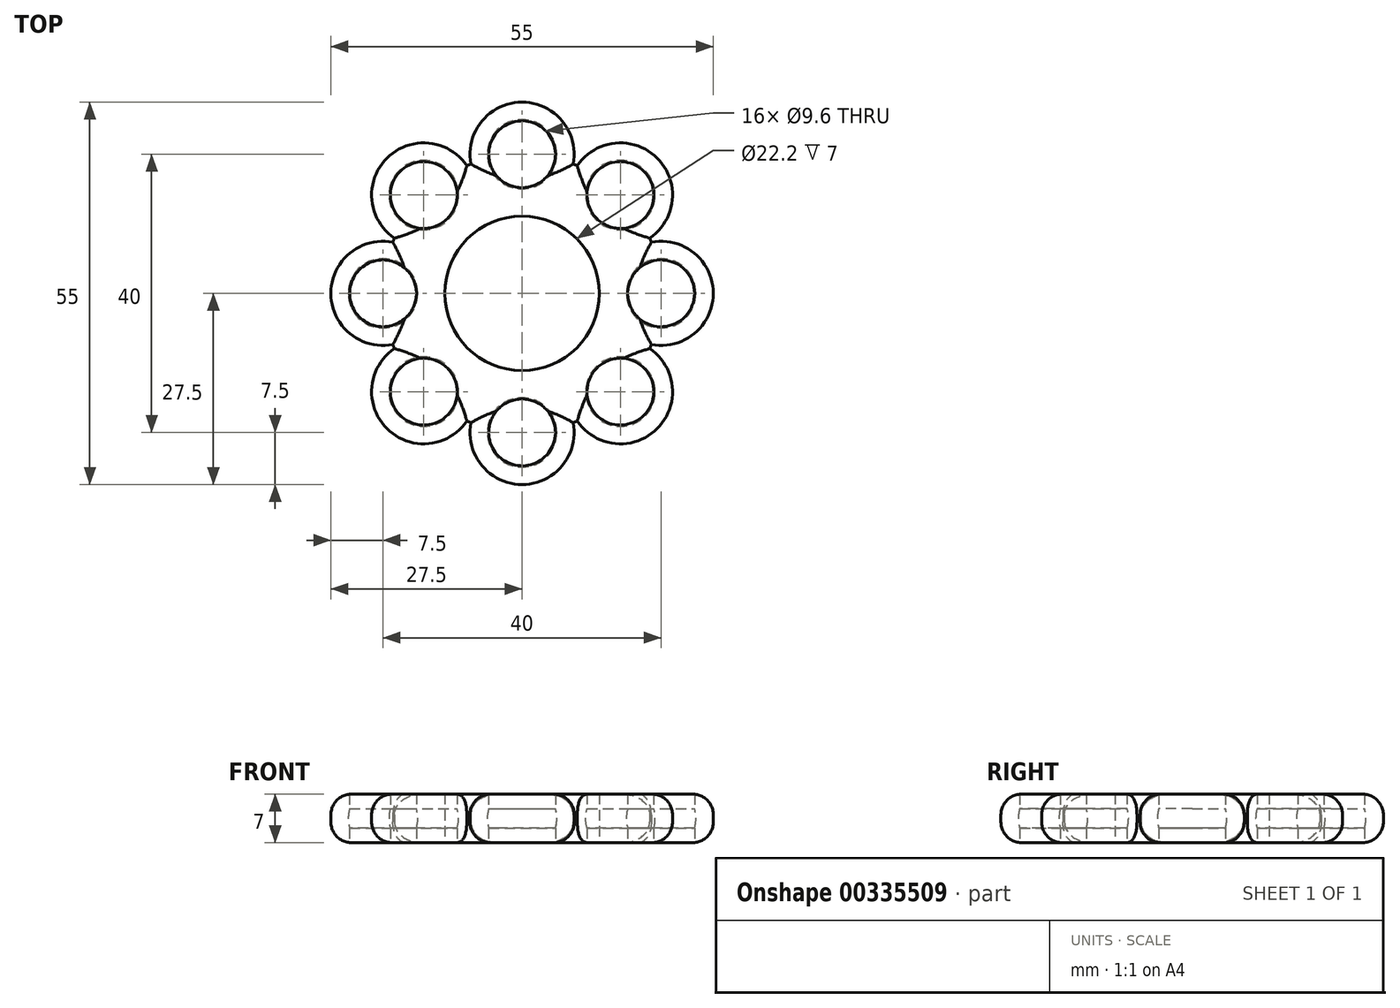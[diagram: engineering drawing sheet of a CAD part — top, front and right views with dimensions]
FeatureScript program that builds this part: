
annotation { "Feature Type Name" : "Feature", "Feature Type Description" : "" }
export const myFeature = defineFeature(function(context is Context, id is Id, definition is map)
    precondition{}
    {
        {
            var Q0;
            Q0=qCreatedBy(makeId("Top.planeOp"),FACE);
            var sketch = newSketch(context, id + "F0", { "sketchPlane" : qUnion([Q0])});
            skCircle(sketch, "E0", {"center": v(0, 0) * mm, "radius": 11.1 * mm});
            skCircle(sketch, "E1", {"center": v(0, 20) * mm, "radius": 4.8 * mm});
            skCircle(sketch, "E2.1.0", {"center": v(-14.14, 14.14) * mm, "radius": 4.8 * mm});
            skCircle(sketch, "E2.2.0", {"center": v(-20, 0) * mm, "radius": 4.8 * mm});
            skCircle(sketch, "E2.3.0", {"center": v(-14.14, -14.14) * mm, "radius": 4.8 * mm});
            skCircle(sketch, "E2.4.0", {"center": v(0, -20) * mm, "radius": 4.8 * mm});
            skCircle(sketch, "E2.5.0", {"center": v(14.14, -14.14) * mm, "radius": 4.8 * mm});
            skCircle(sketch, "E2.6.0", {"center": v(20, 0) * mm, "radius": 4.8 * mm});
            skCircle(sketch, "E2.7.0", {"center": v(14.14, 14.14) * mm, "radius": 4.8 * mm});
            skCircle(sketch, "E3", {"center": v(0, 20) * mm, "radius": 7.5 * mm});
            skCircle(sketch, "E4.1.0", {"center": v(-14.14, 14.14) * mm, "radius": 7.5 * mm});
            skCircle(sketch, "E4.2.0", {"center": v(-20, 0) * mm, "radius": 7.5 * mm});
            skCircle(sketch, "E4.3.0", {"center": v(-14.14, -14.14) * mm, "radius": 7.5 * mm});
            skCircle(sketch, "E4.4.0", {"center": v(0, -20) * mm, "radius": 7.5 * mm});
            skCircle(sketch, "E4.5.0", {"center": v(14.14, -14.14) * mm, "radius": 7.5 * mm});
            skCircle(sketch, "E4.6.0", {"center": v(20, 0) * mm, "radius": 7.5 * mm});
            skCircle(sketch, "E4.7.0", {"center": v(14.14, 14.14) * mm, "radius": 7.5 * mm});
            skCircle(sketch, "E5", {"center": v(0, 0) * mm, "radius": 20 * mm});
            skSolve(sketch);
        }
        {
            var Q0;
            Q0=makeQuery(id+"F0.imprint","IMPRINT",FACE,{"disambiguationData":[TD([[makeQuery(id+"F0.imprint","IMPRINT",EDGE,{"derivedFrom":sQuery(id+"F0.wireOp",EDGE,"E0")}),-1.0]])]});
            var Q1;
            {var subQ0=sQuery(id+"F0.wireOp",EDGE,"E5");var subQ1=sQuery(id+"F0.wireOp",EDGE,"E2.3.0");var subQ2=makeQuery(id+"F0.imprint","INTERSECT",VERTEX,{"disambiguationData":[OD(0.0)],"derivedFrom":[subQ1,subQ0]});Q1=makeQuery(id+"F0.imprint","IMPRINT",FACE,{"disambiguationData":[TD([[makeQuery(id+"F0.imprint","IMPRINT",EDGE,{"disambiguationData":[TD([[subQ2,-1.0]])],"derivedFrom":subQ1}),-1.0]])]});}
            var Q2;
            {var subQ0=sQuery(id+"F0.wireOp",EDGE,"E5");var subQ1=sQuery(id+"F0.wireOp",EDGE,"E2.3.0");var subQ2=makeQuery(id+"F0.imprint","INTERSECT",VERTEX,{"disambiguationData":[OD(0.0)],"derivedFrom":[subQ1,subQ0]});Q2=makeQuery(id+"F0.imprint","IMPRINT",FACE,{"disambiguationData":[TD([[makeQuery(id+"F0.imprint","IMPRINT",EDGE,{"disambiguationData":[TD([[subQ2,1.0]])],"derivedFrom":subQ1}),-1.0]])]});}
            var Q3;
            {var subQ0=sQuery(id+"F0.wireOp",EDGE,"E5");var subQ1=sQuery(id+"F0.wireOp",EDGE,"E2.2.0");var subQ2=makeQuery(id+"F0.imprint","INTERSECT",VERTEX,{"disambiguationData":[OD(0.0)],"derivedFrom":[subQ1,subQ0]});Q3=makeQuery(id+"F0.imprint","IMPRINT",FACE,{"disambiguationData":[TD([[makeQuery(id+"F0.imprint","IMPRINT",EDGE,{"disambiguationData":[TD([[subQ2,1.0]])],"derivedFrom":subQ1}),-1.0]])]});}
            var Q4;
            {var subQ0=sQuery(id+"F0.wireOp",EDGE,"E5");var subQ1=sQuery(id+"F0.wireOp",EDGE,"E2.2.0");var subQ2=makeQuery(id+"F0.imprint","INTERSECT",VERTEX,{"disambiguationData":[OD(0.0)],"derivedFrom":[subQ1,subQ0]});Q4=makeQuery(id+"F0.imprint","IMPRINT",FACE,{"disambiguationData":[TD([[makeQuery(id+"F0.imprint","IMPRINT",EDGE,{"disambiguationData":[TD([[subQ2,-1.0]])],"derivedFrom":subQ1}),-1.0]])]});}
            var Q5;
            {var subQ0=sQuery(id+"F0.wireOp",EDGE,"E5");var subQ1=sQuery(id+"F0.wireOp",EDGE,"E2.1.0");var subQ2=makeQuery(id+"F0.imprint","INTERSECT",VERTEX,{"disambiguationData":[OD(0.0)],"derivedFrom":[subQ1,subQ0]});Q5=makeQuery(id+"F0.imprint","IMPRINT",FACE,{"disambiguationData":[TD([[makeQuery(id+"F0.imprint","IMPRINT",EDGE,{"disambiguationData":[TD([[subQ2,-1.0]])],"derivedFrom":subQ1}),-1.0]])]});}
            var Q6;
            {var subQ0=sQuery(id+"F0.wireOp",EDGE,"E5");var subQ1=sQuery(id+"F0.wireOp",EDGE,"E2.1.0");var subQ2=makeQuery(id+"F0.imprint","INTERSECT",VERTEX,{"disambiguationData":[OD(0.0)],"derivedFrom":[subQ1,subQ0]});Q6=makeQuery(id+"F0.imprint","IMPRINT",FACE,{"disambiguationData":[TD([[makeQuery(id+"F0.imprint","IMPRINT",EDGE,{"disambiguationData":[TD([[subQ2,1.0]])],"derivedFrom":subQ1}),-1.0]])]});}
            var Q7;
            {var subQ0=sQuery(id+"F0.wireOp",EDGE,"E5");var subQ1=sQuery(id+"F0.wireOp",EDGE,"E1");var subQ2=makeQuery(id+"F0.imprint","INTERSECT",VERTEX,{"disambiguationData":[OD(0.0)],"derivedFrom":[subQ1,subQ0]});Q7=makeQuery(id+"F0.imprint","IMPRINT",FACE,{"disambiguationData":[TD([[makeQuery(id+"F0.imprint","IMPRINT",EDGE,{"disambiguationData":[TD([[subQ2,1.0]])],"derivedFrom":subQ1}),-1.0]])]});}
            var Q8;
            {var subQ0=sQuery(id+"F0.wireOp",EDGE,"E5");var subQ1=sQuery(id+"F0.wireOp",EDGE,"E1");var subQ2=makeQuery(id+"F0.imprint","INTERSECT",VERTEX,{"disambiguationData":[OD(0.0)],"derivedFrom":[subQ1,subQ0]});Q8=makeQuery(id+"F0.imprint","IMPRINT",FACE,{"disambiguationData":[TD([[makeQuery(id+"F0.imprint","IMPRINT",EDGE,{"disambiguationData":[TD([[subQ2,-1.0]])],"derivedFrom":subQ1}),-1.0]])]});}
            var Q9;
            {var subQ0=sQuery(id+"F0.wireOp",EDGE,"E5");var subQ1=sQuery(id+"F0.wireOp",EDGE,"E2.7.0");var subQ2=makeQuery(id+"F0.imprint","INTERSECT",VERTEX,{"disambiguationData":[OD(0.0)],"derivedFrom":[subQ1,subQ0]});Q9=makeQuery(id+"F0.imprint","IMPRINT",FACE,{"disambiguationData":[TD([[makeQuery(id+"F0.imprint","IMPRINT",EDGE,{"disambiguationData":[TD([[subQ2,1.0]])],"derivedFrom":subQ1}),-1.0]])]});}
            var Q10;
            {var subQ0=sQuery(id+"F0.wireOp",EDGE,"E5");var subQ1=sQuery(id+"F0.wireOp",EDGE,"E2.7.0");var subQ2=makeQuery(id+"F0.imprint","INTERSECT",VERTEX,{"disambiguationData":[OD(0.0)],"derivedFrom":[subQ1,subQ0]});Q10=makeQuery(id+"F0.imprint","IMPRINT",FACE,{"disambiguationData":[TD([[makeQuery(id+"F0.imprint","IMPRINT",EDGE,{"disambiguationData":[TD([[subQ2,-1.0]])],"derivedFrom":subQ1}),-1.0]])]});}
            var Q11;
            {var subQ0=sQuery(id+"F0.wireOp",EDGE,"E5");var subQ1=sQuery(id+"F0.wireOp",EDGE,"E2.6.0");var subQ2=makeQuery(id+"F0.imprint","INTERSECT",VERTEX,{"disambiguationData":[OD(0.0)],"derivedFrom":[subQ1,subQ0]});Q11=makeQuery(id+"F0.imprint","IMPRINT",FACE,{"disambiguationData":[TD([[makeQuery(id+"F0.imprint","IMPRINT",EDGE,{"disambiguationData":[TD([[subQ2,-1.0]])],"derivedFrom":subQ1}),-1.0]])]});}
            var Q12;
            {var subQ0=sQuery(id+"F0.wireOp",EDGE,"E5");var subQ1=sQuery(id+"F0.wireOp",EDGE,"E2.6.0");var subQ2=makeQuery(id+"F0.imprint","INTERSECT",VERTEX,{"disambiguationData":[OD(0.0)],"derivedFrom":[subQ1,subQ0]});Q12=makeQuery(id+"F0.imprint","IMPRINT",FACE,{"disambiguationData":[TD([[makeQuery(id+"F0.imprint","IMPRINT",EDGE,{"disambiguationData":[TD([[subQ2,1.0]])],"derivedFrom":subQ1}),-1.0]])]});}
            var Q13;
            {var subQ0=sQuery(id+"F0.wireOp",EDGE,"E5");var subQ1=sQuery(id+"F0.wireOp",EDGE,"E2.5.0");var subQ2=makeQuery(id+"F0.imprint","INTERSECT",VERTEX,{"disambiguationData":[OD(0.0)],"derivedFrom":[subQ1,subQ0]});Q13=makeQuery(id+"F0.imprint","IMPRINT",FACE,{"disambiguationData":[TD([[makeQuery(id+"F0.imprint","IMPRINT",EDGE,{"disambiguationData":[TD([[subQ2,1.0]])],"derivedFrom":subQ1}),-1.0]])]});}
            var Q14;
            {var subQ0=sQuery(id+"F0.wireOp",EDGE,"E5");var subQ1=sQuery(id+"F0.wireOp",EDGE,"E2.5.0");var subQ2=makeQuery(id+"F0.imprint","INTERSECT",VERTEX,{"disambiguationData":[OD(0.0)],"derivedFrom":[subQ1,subQ0]});Q14=makeQuery(id+"F0.imprint","IMPRINT",FACE,{"disambiguationData":[TD([[makeQuery(id+"F0.imprint","IMPRINT",EDGE,{"disambiguationData":[TD([[subQ2,-1.0]])],"derivedFrom":subQ1}),-1.0]])]});}
            var Q15;
            {var subQ0=sQuery(id+"F0.wireOp",EDGE,"E5");var subQ1=sQuery(id+"F0.wireOp",EDGE,"E2.4.0");var subQ2=makeQuery(id+"F0.imprint","INTERSECT",VERTEX,{"disambiguationData":[OD(0.0)],"derivedFrom":[subQ1,subQ0]});Q15=makeQuery(id+"F0.imprint","IMPRINT",FACE,{"disambiguationData":[TD([[makeQuery(id+"F0.imprint","IMPRINT",EDGE,{"disambiguationData":[TD([[subQ2,1.0]])],"derivedFrom":subQ1}),-1.0]])]});}
            var Q16;
            {var subQ0=sQuery(id+"F0.wireOp",EDGE,"E5");var subQ1=sQuery(id+"F0.wireOp",EDGE,"E2.4.0");var subQ2=makeQuery(id+"F0.imprint","INTERSECT",VERTEX,{"disambiguationData":[OD(0.0)],"derivedFrom":[subQ1,subQ0]});Q16=makeQuery(id+"F0.imprint","IMPRINT",FACE,{"disambiguationData":[TD([[makeQuery(id+"F0.imprint","IMPRINT",EDGE,{"disambiguationData":[TD([[subQ2,-1.0]])],"derivedFrom":subQ1}),-1.0]])]});}
            extrude(context, id + "F1", {"entities" : qUnion([Q0, Q1, Q2, Q3, Q4, Q5, Q6, Q7, Q8, Q9, Q10, Q11, Q12, Q13, Q14, Q15, Q16]), "depth" : 3.5 * mm, "hasSecondDirection" : true, "secondDirectionOppositeDirection" : true, "secondDirectionDepth" : 3.5 * mm});
        }
        {
            var Q0;
            Q0=makeQuery(id+"F1.opExtrude","CAP_EDGE",EDGE,{"disambiguationData":[OSD([sQuery(id+"F0.wireOp",EDGE,"E4.7.0")])],"isStart":false});
            var Q1;
            Q1=makeQuery(id+"F1.opExtrude","CAP_EDGE",EDGE,{"disambiguationData":[OSD([sQuery(id+"F0.wireOp",EDGE,"E4.7.0")])],"isStart":true});
            var Q2;
            Q2=makeQuery(id+"F1.opExtrude","CAP_EDGE",EDGE,{"disambiguationData":[OSD([sQuery(id+"F0.wireOp",EDGE,"E3")])],"isStart":false});
            var Q3;
            {var subQ0=sQuery(id+"F0.wireOp",EDGE,"E5");Q3=makeQuery(id+"F1.opExtrude","CAP_EDGE",EDGE,{"disambiguationData":[OSD([subQ0]),TDD([makeQuery(id+"F0.imprint","IMPRINT",EDGE,{"disambiguationData":[TD([[makeQuery(id+"F0.imprint","INTERSECT",VERTEX,{"disambiguationData":[OD(0.0)],"derivedFrom":[sQuery(id+"F0.wireOp",EDGE,"E3"),subQ0]}),1.0]])],"derivedFrom":subQ0})])],"isStart":false});}
            var Q4;
            Q4=makeQuery(id+"F1.opExtrude","CAP_EDGE",EDGE,{"disambiguationData":[OSD([sQuery(id+"F0.wireOp",EDGE,"E4.6.0")])],"isStart":false});
            var Q5;
            {var subQ0=sQuery(id+"F0.wireOp",EDGE,"E5");Q5=makeQuery(id+"F1.opExtrude","CAP_EDGE",EDGE,{"disambiguationData":[OSD([subQ0]),TDD([makeQuery(id+"F0.imprint","IMPRINT",EDGE,{"disambiguationData":[TD([[makeQuery(id+"F0.imprint","INTERSECT",VERTEX,{"disambiguationData":[OD(0.0)],"derivedFrom":[sQuery(id+"F0.wireOp",EDGE,"E4.6.0"),subQ0]}),-1.0]])],"derivedFrom":subQ0})])],"isStart":false});}
            var Q6;
            Q6=makeQuery(id+"F1.opExtrude","CAP_EDGE",EDGE,{"disambiguationData":[OSD([sQuery(id+"F0.wireOp",EDGE,"E4.1.0")])],"isStart":false});
            var Q7;
            {var subQ0=sQuery(id+"F0.wireOp",EDGE,"E5");Q7=makeQuery(id+"F1.opExtrude","CAP_EDGE",EDGE,{"disambiguationData":[OSD([subQ0]),TDD([makeQuery(id+"F0.imprint","IMPRINT",EDGE,{"disambiguationData":[TD([[makeQuery(id+"F0.imprint","INTERSECT",VERTEX,{"disambiguationData":[OD(1.0)],"derivedFrom":[sQuery(id+"F0.wireOp",EDGE,"E3"),subQ0]}),-1.0]])],"derivedFrom":subQ0})])],"isStart":false});}
            var Q8;
            Q8=makeQuery(id+"F1.opExtrude","CAP_EDGE",EDGE,{"disambiguationData":[OSD([sQuery(id+"F0.wireOp",EDGE,"E4.2.0")])],"isStart":false});
            var Q9;
            Q9=makeQuery(id+"F1.opExtrude","CAP_EDGE",EDGE,{"disambiguationData":[OSD([sQuery(id+"F0.wireOp",EDGE,"E4.3.0")])],"isStart":false});
            var Q10;
            Q10=makeQuery(id+"F1.opExtrude","CAP_EDGE",EDGE,{"disambiguationData":[OSD([sQuery(id+"F0.wireOp",EDGE,"E4.4.0")])],"isStart":false});
            var Q11;
            Q11=makeQuery(id+"F1.opExtrude","CAP_EDGE",EDGE,{"disambiguationData":[OSD([sQuery(id+"F0.wireOp",EDGE,"E4.5.0")])],"isStart":false});
            var Q12;
            {var subQ0=sQuery(id+"F0.wireOp",EDGE,"E5");Q12=makeQuery(id+"F1.opExtrude","CAP_EDGE",EDGE,{"disambiguationData":[OSD([subQ0]),TDD([makeQuery(id+"F0.imprint","IMPRINT",EDGE,{"disambiguationData":[TD([[makeQuery(id+"F0.imprint","INTERSECT",VERTEX,{"disambiguationData":[OD(1.0)],"derivedFrom":[sQuery(id+"F0.wireOp",EDGE,"E4.5.0"),subQ0]}),-1.0]])],"derivedFrom":subQ0})])],"isStart":false});}
            var Q13;
            {var subQ0=sQuery(id+"F0.wireOp",EDGE,"E5");Q13=makeQuery(id+"F1.opExtrude","CAP_EDGE",EDGE,{"disambiguationData":[OSD([subQ0]),TDD([makeQuery(id+"F0.imprint","IMPRINT",EDGE,{"disambiguationData":[TD([[makeQuery(id+"F0.imprint","INTERSECT",VERTEX,{"disambiguationData":[OD(1.0)],"derivedFrom":[sQuery(id+"F0.wireOp",EDGE,"E4.4.0"),subQ0]}),-1.0]])],"derivedFrom":subQ0})])],"isStart":false});}
            var Q14;
            {var subQ0=sQuery(id+"F0.wireOp",EDGE,"E5");Q14=makeQuery(id+"F1.opExtrude","CAP_EDGE",EDGE,{"disambiguationData":[OSD([subQ0]),TDD([makeQuery(id+"F0.imprint","IMPRINT",EDGE,{"disambiguationData":[TD([[makeQuery(id+"F0.imprint","INTERSECT",VERTEX,{"disambiguationData":[OD(1.0)],"derivedFrom":[sQuery(id+"F0.wireOp",EDGE,"E4.3.0"),subQ0]}),-1.0]])],"derivedFrom":subQ0})])],"isStart":false});}
            var Q15;
            {var subQ0=sQuery(id+"F0.wireOp",EDGE,"E5");Q15=makeQuery(id+"F1.opExtrude","CAP_EDGE",EDGE,{"disambiguationData":[OSD([subQ0]),TDD([makeQuery(id+"F0.imprint","IMPRINT",EDGE,{"disambiguationData":[TD([[makeQuery(id+"F0.imprint","INTERSECT",VERTEX,{"disambiguationData":[OD(1.0)],"derivedFrom":[sQuery(id+"F0.wireOp",EDGE,"E4.2.0"),subQ0]}),-1.0]])],"derivedFrom":subQ0})])],"isStart":false});}
            var Q16;
            {var subQ0=sQuery(id+"F0.wireOp",EDGE,"E5");Q16=makeQuery(id+"F1.opExtrude","CAP_EDGE",EDGE,{"disambiguationData":[OSD([subQ0]),TDD([makeQuery(id+"F0.imprint","IMPRINT",EDGE,{"disambiguationData":[TD([[makeQuery(id+"F0.imprint","INTERSECT",VERTEX,{"disambiguationData":[OD(1.0)],"derivedFrom":[sQuery(id+"F0.wireOp",EDGE,"E4.1.0"),subQ0]}),-1.0]])],"derivedFrom":subQ0})])],"isStart":false});}
            var Q17;
            Q17=makeQuery(id+"F1.opExtrude","CAP_EDGE",EDGE,{"disambiguationData":[OSD([sQuery(id+"F0.wireOp",EDGE,"E4.3.0")])],"isStart":true});
            var Q18;
            Q18=makeQuery(id+"F1.opExtrude","CAP_EDGE",EDGE,{"disambiguationData":[OSD([sQuery(id+"F0.wireOp",EDGE,"E4.4.0")])],"isStart":true});
            var Q19;
            Q19=makeQuery(id+"F1.opExtrude","CAP_EDGE",EDGE,{"disambiguationData":[OSD([sQuery(id+"F0.wireOp",EDGE,"E4.2.0")])],"isStart":true});
            var Q20;
            Q20=makeQuery(id+"F1.opExtrude","CAP_EDGE",EDGE,{"disambiguationData":[OSD([sQuery(id+"F0.wireOp",EDGE,"E4.1.0")])],"isStart":true});
            var Q21;
            Q21=makeQuery(id+"F1.opExtrude","CAP_EDGE",EDGE,{"disambiguationData":[OSD([sQuery(id+"F0.wireOp",EDGE,"E3")])],"isStart":true});
            var Q22;
            Q22=makeQuery(id+"F1.opExtrude","CAP_EDGE",EDGE,{"disambiguationData":[OSD([sQuery(id+"F0.wireOp",EDGE,"E4.6.0")])],"isStart":true});
            var Q23;
            Q23=makeQuery(id+"F1.opExtrude","CAP_EDGE",EDGE,{"disambiguationData":[OSD([sQuery(id+"F0.wireOp",EDGE,"E4.5.0")])],"isStart":true});
            var Q24;
            {var subQ0=sQuery(id+"F0.wireOp",EDGE,"E5");Q24=makeQuery(id+"F1.opExtrude","CAP_EDGE",EDGE,{"disambiguationData":[OSD([subQ0]),TDD([makeQuery(id+"F0.imprint","IMPRINT",EDGE,{"disambiguationData":[TD([[makeQuery(id+"F0.imprint","INTERSECT",VERTEX,{"disambiguationData":[OD(1.0)],"derivedFrom":[sQuery(id+"F0.wireOp",EDGE,"E4.3.0"),subQ0]}),-1.0]])],"derivedFrom":subQ0})])],"isStart":true});}
            var Q25;
            {var subQ0=sQuery(id+"F0.wireOp",EDGE,"E5");Q25=makeQuery(id+"F1.opExtrude","CAP_EDGE",EDGE,{"disambiguationData":[OSD([subQ0]),TDD([makeQuery(id+"F0.imprint","IMPRINT",EDGE,{"disambiguationData":[TD([[makeQuery(id+"F0.imprint","INTERSECT",VERTEX,{"disambiguationData":[OD(1.0)],"derivedFrom":[sQuery(id+"F0.wireOp",EDGE,"E4.4.0"),subQ0]}),-1.0]])],"derivedFrom":subQ0})])],"isStart":true});}
            var Q26;
            {var subQ0=sQuery(id+"F0.wireOp",EDGE,"E5");Q26=makeQuery(id+"F1.opExtrude","CAP_EDGE",EDGE,{"disambiguationData":[OSD([subQ0]),TDD([makeQuery(id+"F0.imprint","IMPRINT",EDGE,{"disambiguationData":[TD([[makeQuery(id+"F0.imprint","INTERSECT",VERTEX,{"disambiguationData":[OD(1.0)],"derivedFrom":[sQuery(id+"F0.wireOp",EDGE,"E4.2.0"),subQ0]}),-1.0]])],"derivedFrom":subQ0})])],"isStart":true});}
            var Q27;
            {var subQ0=sQuery(id+"F0.wireOp",EDGE,"E5");Q27=makeQuery(id+"F1.opExtrude","CAP_EDGE",EDGE,{"disambiguationData":[OSD([subQ0]),TDD([makeQuery(id+"F0.imprint","IMPRINT",EDGE,{"disambiguationData":[TD([[makeQuery(id+"F0.imprint","INTERSECT",VERTEX,{"disambiguationData":[OD(1.0)],"derivedFrom":[sQuery(id+"F0.wireOp",EDGE,"E4.1.0"),subQ0]}),-1.0]])],"derivedFrom":subQ0})])],"isStart":true});}
            var Q28;
            {var subQ0=sQuery(id+"F0.wireOp",EDGE,"E5");Q28=makeQuery(id+"F1.opExtrude","CAP_EDGE",EDGE,{"disambiguationData":[OSD([subQ0]),TDD([makeQuery(id+"F0.imprint","IMPRINT",EDGE,{"disambiguationData":[TD([[makeQuery(id+"F0.imprint","INTERSECT",VERTEX,{"disambiguationData":[OD(1.0)],"derivedFrom":[sQuery(id+"F0.wireOp",EDGE,"E3"),subQ0]}),-1.0]])],"derivedFrom":subQ0})])],"isStart":true});}
            var Q29;
            {var subQ0=sQuery(id+"F0.wireOp",EDGE,"E5");Q29=makeQuery(id+"F1.opExtrude","CAP_EDGE",EDGE,{"disambiguationData":[OSD([subQ0]),TDD([makeQuery(id+"F0.imprint","IMPRINT",EDGE,{"disambiguationData":[TD([[makeQuery(id+"F0.imprint","INTERSECT",VERTEX,{"disambiguationData":[OD(0.0)],"derivedFrom":[sQuery(id+"F0.wireOp",EDGE,"E3"),subQ0]}),1.0]])],"derivedFrom":subQ0})])],"isStart":true});}
            var Q30;
            {var subQ0=sQuery(id+"F0.wireOp",EDGE,"E5");Q30=makeQuery(id+"F1.opExtrude","CAP_EDGE",EDGE,{"disambiguationData":[OSD([subQ0]),TDD([makeQuery(id+"F0.imprint","IMPRINT",EDGE,{"disambiguationData":[TD([[makeQuery(id+"F0.imprint","INTERSECT",VERTEX,{"disambiguationData":[OD(0.0)],"derivedFrom":[sQuery(id+"F0.wireOp",EDGE,"E4.6.0"),subQ0]}),-1.0]])],"derivedFrom":subQ0})])],"isStart":true});}
            var Q31;
            {var subQ0=sQuery(id+"F0.wireOp",EDGE,"E5");Q31=makeQuery(id+"F1.opExtrude","CAP_EDGE",EDGE,{"disambiguationData":[OSD([subQ0]),TDD([makeQuery(id+"F0.imprint","IMPRINT",EDGE,{"disambiguationData":[TD([[makeQuery(id+"F0.imprint","INTERSECT",VERTEX,{"disambiguationData":[OD(1.0)],"derivedFrom":[sQuery(id+"F0.wireOp",EDGE,"E4.5.0"),subQ0]}),-1.0]])],"derivedFrom":subQ0})])],"isStart":true});}
            fillet(context, id + "F2", {"entities" : qUnion([Q0, Q1, Q2, Q3, Q4, Q5, Q6, Q7, Q8, Q9, Q10, Q11, Q12, Q13, Q14, Q15, Q16, Q17, Q18, Q19, Q20, Q21, Q22, Q23, Q24, Q25, Q26, Q27, Q28, Q29, Q30, Q31]), "radius" : 3 * mm, "tangentPropagation" : true, "allowEdgeOverflow" : false});
        }
        {
            var Q0;
            Q0=qCreatedBy(makeId("Right.planeOp"),FACE);
            var sketch = newSketch(context, id + "F3", { "sketchPlane" : qUnion([Q0])});
            skPoint(sketch, "E6.0", {"position": v(-20, 0) * mm});
            skPoint(sketch, "E6.1", {"position": v(20, 0) * mm});
            skLineSegment(sketch, "E7", {"start": v(-20, 13.32) * mm, "end": v(-20, -12.27) * mm, "construction": true});
            skLineSegment(sketch, "E8", {"start": v(20, 13.15) * mm, "end": v(20, -12.27) * mm, "construction": true});
            skPoint(sketch, "E9", {"position": v(-20, 5) * mm});
            skPoint(sketch, "E10", {"position": v(-20, -5) * mm});
            skPoint(sketch, "E11", {"position": v(20, 5) * mm});
            skPoint(sketch, "E12", {"position": v(20, -5) * mm});
            skArc(sketch, "E13", {"start": v(-20, 5) * mm, "mid": v(-25, 0) * mm, "end": v(-20, -5) * mm});
            skArc(sketch, "E14", {"start": v(20, -5) * mm, "mid": v(25, 0) * mm, "end": v(20, 5) * mm});
            skLineSegment(sketch, "E15", {"start": v(-20, 5) * mm, "end": v(-20, -5) * mm});
            skLineSegment(sketch, "E16", {"start": v(20, 5) * mm, "end": v(20, -5) * mm});
            skLineSegment(sketch, "E17", {"start": v(0, 41.23) * mm, "end": v(0, -49.38) * mm, "construction": true});
            skSolve(sketch);
        }
        {
            var Q0;
            Q0=makeQuery(id+"F3.imprint","IMPRINT",FACE,{"disambiguationData":[TD([[makeQuery(id+"F3.imprint","IMPRINT",EDGE,{"derivedFrom":sQuery(id+"F3.wireOp",EDGE,"E13")}),1.0]])]});
            var Q1;
            Q1=sQuery(id+"F3.wireOp",EDGE,"E7");
            revolve(context, id + "F4", {"entities" : qUnion([Q0]), "axis" : qUnion([Q1]), "revolveType" : RevolveType.FULL});
        }
        {
            var Q0;
            Q0=makeQuery(id+"F3.imprint","IMPRINT",FACE,{"disambiguationData":[TD([[makeQuery(id+"F3.imprint","IMPRINT",EDGE,{"derivedFrom":sQuery(id+"F3.wireOp",EDGE,"E14")}),1.0]])]});
            var Q1;
            Q1=sQuery(id+"F3.wireOp",EDGE,"E8");
            revolve(context, id + "F5", {"entities" : qUnion([Q0]), "axis" : qUnion([Q1]), "revolveType" : RevolveType.FULL});
        }
        {
            var Q0;
            Q0=makeQuery(id+"F5.opRevolve","SWEPT_BODY",BODY,{"disambiguationData":[OSD([sQuery(id+"F3.wireOp",EDGE,"E14"),sQuery(id+"F3.wireOp",EDGE,"E16")])]});
            var Q1;
            Q1=makeQuery(id+"F4.opRevolve","SWEPT_BODY",BODY,{"disambiguationData":[OSD([sQuery(id+"F3.wireOp",EDGE,"E13"),sQuery(id+"F3.wireOp",EDGE,"E15")])]});
            var Q2;
            Q2=makeQuery(id+"F1.opExtrude","SWEPT_BODY",BODY,{"disambiguationData":[OSD([sQuery(id+"F0.wireOp",EDGE,"E0"),sQuery(id+"F0.wireOp",EDGE,"E1"),sQuery(id+"F0.wireOp",EDGE,"E2.1.0"),sQuery(id+"F0.wireOp",EDGE,"E2.2.0"),sQuery(id+"F0.wireOp",EDGE,"E2.3.0"),sQuery(id+"F0.wireOp",EDGE,"E2.4.0"),sQuery(id+"F0.wireOp",EDGE,"E2.5.0"),sQuery(id+"F0.wireOp",EDGE,"E2.6.0"),sQuery(id+"F0.wireOp",EDGE,"E2.7.0"),sQuery(id+"F0.wireOp",EDGE,"E3"),sQuery(id+"F0.wireOp",EDGE,"E4.1.0"),sQuery(id+"F0.wireOp",EDGE,"E4.2.0"),sQuery(id+"F0.wireOp",EDGE,"E4.3.0"),sQuery(id+"F0.wireOp",EDGE,"E4.4.0"),sQuery(id+"F0.wireOp",EDGE,"E4.5.0"),sQuery(id+"F0.wireOp",EDGE,"E4.6.0"),sQuery(id+"F0.wireOp",EDGE,"E4.7.0"),sQuery(id+"F0.wireOp",EDGE,"E5")])]});
            booleanBodies(context, id + "F6", {"operationType" : BooleanOperationType.SUBTRACTION, "tools" : qUnion([Q0, Q1]), "targets" : qUnion([Q2])});
        }
        {
            var Q0;
            Q0=qCreatedBy(makeId("Front.planeOp"),FACE);
            var sketch = newSketch(context, id + "F7", { "sketchPlane" : qUnion([Q0])});
            skPoint(sketch, "E18.0", {"position": v(-20, 0) * mm});
            skPoint(sketch, "E18.1", {"position": v(20, 0) * mm});
            skLineSegment(sketch, "E19", {"start": v(-20, 19.56) * mm, "end": v(-20, -19.6) * mm, "construction": true});
            skLineSegment(sketch, "E20", {"start": v(20, 20.64) * mm, "end": v(20, -20.78) * mm, "construction": true});
            skPoint(sketch, "E21", {"position": v(-20, 5) * mm});
            skPoint(sketch, "E22", {"position": v(-20, -5) * mm});
            skPoint(sketch, "E23", {"position": v(20, 5) * mm});
            skPoint(sketch, "E24", {"position": v(20, -5) * mm});
            skArc(sketch, "E25", {"start": v(-20, 5) * mm, "mid": v(-25, 0) * mm, "end": v(-20, -5) * mm});
            skArc(sketch, "E26", {"start": v(20, -5) * mm, "mid": v(25, 0) * mm, "end": v(20, 5) * mm});
            skLineSegment(sketch, "E27", {"start": v(-20, 5) * mm, "end": v(-20, -5) * mm});
            skLineSegment(sketch, "E28", {"start": v(20, 5) * mm, "end": v(20, -5) * mm});
            skSolve(sketch);
        }
        {
            var Q0;
            Q0=makeQuery(id+"F7.imprint","IMPRINT",FACE,{"disambiguationData":[TD([[makeQuery(id+"F7.imprint","IMPRINT",EDGE,{"derivedFrom":sQuery(id+"F7.wireOp",EDGE,"E25")}),1.0]])]});
            var Q1;
            Q1=sQuery(id+"F7.wireOp",EDGE,"E19");
            revolve(context, id + "F8", {"entities" : qUnion([Q0]), "axis" : qUnion([Q1]), "revolveType" : RevolveType.FULL});
        }
        {
            var Q0;
            Q0=makeQuery(id+"F7.imprint","IMPRINT",FACE,{"disambiguationData":[TD([[makeQuery(id+"F7.imprint","IMPRINT",EDGE,{"derivedFrom":sQuery(id+"F7.wireOp",EDGE,"E26")}),1.0]])]});
            var Q1;
            Q1=sQuery(id+"F7.wireOp",EDGE,"E20");
            revolve(context, id + "F9", {"entities" : qUnion([Q0]), "axis" : qUnion([Q1]), "revolveType" : RevolveType.FULL});
        }
        {
            var Q0;
            Q0=makeQuery(id+"F8.opRevolve","SWEPT_BODY",BODY,{"disambiguationData":[OSD([sQuery(id+"F7.wireOp",EDGE,"E25"),sQuery(id+"F7.wireOp",EDGE,"E27")])]});
            var Q1;
            Q1=makeQuery(id+"F9.opRevolve","SWEPT_BODY",BODY,{"disambiguationData":[OSD([sQuery(id+"F7.wireOp",EDGE,"E26"),sQuery(id+"F7.wireOp",EDGE,"E28")])]});
            var Q2;
            Q2=makeQuery(id+"F1.opExtrude","SWEPT_BODY",BODY,{"disambiguationData":[OSD([sQuery(id+"F0.wireOp",EDGE,"E0"),sQuery(id+"F0.wireOp",EDGE,"E1"),sQuery(id+"F0.wireOp",EDGE,"E2.1.0"),sQuery(id+"F0.wireOp",EDGE,"E2.2.0"),sQuery(id+"F0.wireOp",EDGE,"E2.3.0"),sQuery(id+"F0.wireOp",EDGE,"E2.4.0"),sQuery(id+"F0.wireOp",EDGE,"E2.5.0"),sQuery(id+"F0.wireOp",EDGE,"E2.6.0"),sQuery(id+"F0.wireOp",EDGE,"E2.7.0"),sQuery(id+"F0.wireOp",EDGE,"E3"),sQuery(id+"F0.wireOp",EDGE,"E4.1.0"),sQuery(id+"F0.wireOp",EDGE,"E4.2.0"),sQuery(id+"F0.wireOp",EDGE,"E4.3.0"),sQuery(id+"F0.wireOp",EDGE,"E4.4.0"),sQuery(id+"F0.wireOp",EDGE,"E4.5.0"),sQuery(id+"F0.wireOp",EDGE,"E4.6.0"),sQuery(id+"F0.wireOp",EDGE,"E4.7.0"),sQuery(id+"F0.wireOp",EDGE,"E5")])]});
            booleanBodies(context, id + "F10", {"operationType" : BooleanOperationType.SUBTRACTION, "tools" : qUnion([Q0, Q1]), "targets" : qUnion([Q2])});
        }
        {
            var Q0;
            Q0=qCreatedBy(makeId("Front.planeOp"),FACE);
            var Q1;
            Q1=sQuery(id+"F0.wireOp",VERTEX,"E2.3.0.center");
            cPlane(context, id + "F11", {"entities" : qUnion([Q0, Q1]), "cplaneType" : CPlaneType.PLANE_POINT, "offset" : 25 * mm, "width" : 150 * mm, "height" : 150 * mm});
        }
        {
            var Q0;
            Q0=qCreatedBy(id+"F11.planeOp",FACE);
            var sketch = newSketch(context, id + "F12", { "sketchPlane" : qUnion([Q0])});
            skPoint(sketch, "E29.0", {"position": v(-14.14, 0) * mm});
            skPoint(sketch, "E29.1", {"position": v(14.14, 0) * mm});
            skLineSegment(sketch, "E30", {"start": v(-14.14, 21.06) * mm, "end": v(-14.14, -25.17) * mm, "construction": true});
            skLineSegment(sketch, "E31", {"start": v(14.14, 18.59) * mm, "end": v(14.14, -22.25) * mm, "construction": true});
            skPoint(sketch, "E32", {"position": v(-14.14, 5) * mm});
            skPoint(sketch, "E33", {"position": v(-14.14, -5) * mm});
            skPoint(sketch, "E34", {"position": v(14.14, -5) * mm});
            skPoint(sketch, "E35", {"position": v(14.14, 5) * mm});
            skArc(sketch, "E36", {"start": v(-14.14, 5) * mm, "mid": v(-19.14, 0) * mm, "end": v(-14.14, -5) * mm});
            skArc(sketch, "E37", {"start": v(14.14, -5) * mm, "mid": v(19.14, 0) * mm, "end": v(14.14, 5) * mm});
            skLineSegment(sketch, "E38", {"start": v(-14.14, 5) * mm, "end": v(-14.14, -5) * mm});
            skLineSegment(sketch, "E39", {"start": v(14.14, 5) * mm, "end": v(14.14, -5) * mm});
            skSolve(sketch);
        }
        {
            var Q0;
            Q0=makeQuery(id+"F12.imprint","IMPRINT",FACE,{"disambiguationData":[TD([[makeQuery(id+"F12.imprint","IMPRINT",EDGE,{"derivedFrom":sQuery(id+"F12.wireOp",EDGE,"E36")}),1.0]])]});
            var Q1;
            Q1=sQuery(id+"F12.wireOp",EDGE,"E30");
            revolve(context, id + "F13", {"entities" : qUnion([Q0]), "axis" : qUnion([Q1]), "revolveType" : RevolveType.FULL});
        }
        {
            var Q0;
            Q0=makeQuery(id+"F12.imprint","IMPRINT",FACE,{"disambiguationData":[TD([[makeQuery(id+"F12.imprint","IMPRINT",EDGE,{"derivedFrom":sQuery(id+"F12.wireOp",EDGE,"E37")}),1.0]])]});
            var Q1;
            Q1=sQuery(id+"F12.wireOp",EDGE,"E31");
            revolve(context, id + "F14", {"entities" : qUnion([Q0]), "axis" : qUnion([Q1]), "revolveType" : RevolveType.FULL});
        }
        {
            var Q0;
            Q0=makeQuery(id+"F14.opRevolve","SWEPT_BODY",BODY,{"disambiguationData":[OSD([sQuery(id+"F12.wireOp",EDGE,"E37"),sQuery(id+"F12.wireOp",EDGE,"E39")])]});
            var Q1;
            Q1=makeQuery(id+"F13.opRevolve","SWEPT_BODY",BODY,{"disambiguationData":[OSD([sQuery(id+"F12.wireOp",EDGE,"E36"),sQuery(id+"F12.wireOp",EDGE,"E38")])]});
            var Q2;
            Q2=makeQuery(id+"F1.opExtrude","SWEPT_BODY",BODY,{"disambiguationData":[OSD([sQuery(id+"F0.wireOp",EDGE,"E0"),sQuery(id+"F0.wireOp",EDGE,"E1"),sQuery(id+"F0.wireOp",EDGE,"E2.1.0"),sQuery(id+"F0.wireOp",EDGE,"E2.2.0"),sQuery(id+"F0.wireOp",EDGE,"E2.3.0"),sQuery(id+"F0.wireOp",EDGE,"E2.4.0"),sQuery(id+"F0.wireOp",EDGE,"E2.5.0"),sQuery(id+"F0.wireOp",EDGE,"E2.6.0"),sQuery(id+"F0.wireOp",EDGE,"E2.7.0"),sQuery(id+"F0.wireOp",EDGE,"E3"),sQuery(id+"F0.wireOp",EDGE,"E4.1.0"),sQuery(id+"F0.wireOp",EDGE,"E4.2.0"),sQuery(id+"F0.wireOp",EDGE,"E4.3.0"),sQuery(id+"F0.wireOp",EDGE,"E4.4.0"),sQuery(id+"F0.wireOp",EDGE,"E4.5.0"),sQuery(id+"F0.wireOp",EDGE,"E4.6.0"),sQuery(id+"F0.wireOp",EDGE,"E4.7.0"),sQuery(id+"F0.wireOp",EDGE,"E5")])]});
            booleanBodies(context, id + "F15", {"operationType" : BooleanOperationType.SUBTRACTION, "tools" : qUnion([Q0, Q1]), "targets" : qUnion([Q2])});
        }
        {
            var Q0;
            Q0=qCreatedBy(makeId("Front.planeOp"),FACE);
            var Q1;
            Q1=sQuery(id+"F0.wireOp",VERTEX,"E4.7.0.center");
            cPlane(context, id + "F16", {"entities" : qUnion([Q0, Q1]), "cplaneType" : CPlaneType.PLANE_POINT, "offset" : 25 * mm, "width" : 150 * mm, "height" : 150 * mm});
        }
        {
            var Q0;
            Q0=qCreatedBy(id+"F16.planeOp",FACE);
            var sketch = newSketch(context, id + "F17", { "sketchPlane" : qUnion([Q0])});
            skPoint(sketch, "E40.0", {"position": v(14.14, 0) * mm});
            skPoint(sketch, "E40.1", {"position": v(-14.14, 0) * mm});
            skLineSegment(sketch, "E41", {"start": v(14.14, 20.99) * mm, "end": v(14.14, -18.6) * mm, "construction": true});
            skLineSegment(sketch, "E42", {"start": v(-14.14, 22.52) * mm, "end": v(-14.14, -18.6) * mm, "construction": true});
            skPoint(sketch, "E43", {"position": v(14.14, 5) * mm});
            skPoint(sketch, "E44", {"position": v(-14.14, 5) * mm});
            skPoint(sketch, "E45", {"position": v(14.14, -5) * mm});
            skPoint(sketch, "E46", {"position": v(-14.14, -5) * mm});
            skArc(sketch, "E47", {"start": v(14.14, -5) * mm, "mid": v(19.14, 0) * mm, "end": v(14.14, 5) * mm});
            skArc(sketch, "E48", {"start": v(-14.14, 5) * mm, "mid": v(-19.14, 0) * mm, "end": v(-14.14, -5) * mm});
            skLineSegment(sketch, "E49", {"start": v(14.14, 5) * mm, "end": v(14.14, -5) * mm});
            skLineSegment(sketch, "E50", {"start": v(-14.14, 5) * mm, "end": v(-14.14, -5) * mm});
            skSolve(sketch);
        }
        {
            var Q0;
            Q0=makeQuery(id+"F17.imprint","IMPRINT",FACE,{"disambiguationData":[TD([[makeQuery(id+"F17.imprint","IMPRINT",EDGE,{"derivedFrom":sQuery(id+"F17.wireOp",EDGE,"E47")}),1.0]])]});
            var Q1;
            Q1=sQuery(id+"F17.wireOp",EDGE,"E41");
            revolve(context, id + "F18", {"entities" : qUnion([Q0]), "axis" : qUnion([Q1]), "revolveType" : RevolveType.FULL});
        }
        {
            var Q0;
            Q0=makeQuery(id+"F17.imprint","IMPRINT",FACE,{"disambiguationData":[TD([[makeQuery(id+"F17.imprint","IMPRINT",EDGE,{"derivedFrom":sQuery(id+"F17.wireOp",EDGE,"E48")}),1.0]])]});
            var Q1;
            Q1=sQuery(id+"F17.wireOp",EDGE,"E42");
            revolve(context, id + "F19", {"entities" : qUnion([Q0]), "axis" : qUnion([Q1]), "revolveType" : RevolveType.FULL});
        }
        {
            var Q0;
            Q0=makeQuery(id+"F19.opRevolve","SWEPT_BODY",BODY,{"disambiguationData":[OSD([sQuery(id+"F17.wireOp",EDGE,"E48"),sQuery(id+"F17.wireOp",EDGE,"E50")])]});
            var Q1;
            Q1=makeQuery(id+"F18.opRevolve","SWEPT_BODY",BODY,{"disambiguationData":[OSD([sQuery(id+"F17.wireOp",EDGE,"E47"),sQuery(id+"F17.wireOp",EDGE,"E49")])]});
            var Q2;
            Q2=makeQuery(id+"F1.opExtrude","SWEPT_BODY",BODY,{"disambiguationData":[OSD([sQuery(id+"F0.wireOp",EDGE,"E0"),sQuery(id+"F0.wireOp",EDGE,"E1"),sQuery(id+"F0.wireOp",EDGE,"E2.1.0"),sQuery(id+"F0.wireOp",EDGE,"E2.2.0"),sQuery(id+"F0.wireOp",EDGE,"E2.3.0"),sQuery(id+"F0.wireOp",EDGE,"E2.4.0"),sQuery(id+"F0.wireOp",EDGE,"E2.5.0"),sQuery(id+"F0.wireOp",EDGE,"E2.6.0"),sQuery(id+"F0.wireOp",EDGE,"E2.7.0"),sQuery(id+"F0.wireOp",EDGE,"E3"),sQuery(id+"F0.wireOp",EDGE,"E4.1.0"),sQuery(id+"F0.wireOp",EDGE,"E4.2.0"),sQuery(id+"F0.wireOp",EDGE,"E4.3.0"),sQuery(id+"F0.wireOp",EDGE,"E4.4.0"),sQuery(id+"F0.wireOp",EDGE,"E4.5.0"),sQuery(id+"F0.wireOp",EDGE,"E4.6.0"),sQuery(id+"F0.wireOp",EDGE,"E4.7.0"),sQuery(id+"F0.wireOp",EDGE,"E5")])]});
            booleanBodies(context, id + "F20", {"operationType" : BooleanOperationType.SUBTRACTION, "tools" : qUnion([Q0, Q1]), "targets" : qUnion([Q2])});
        }
    });
